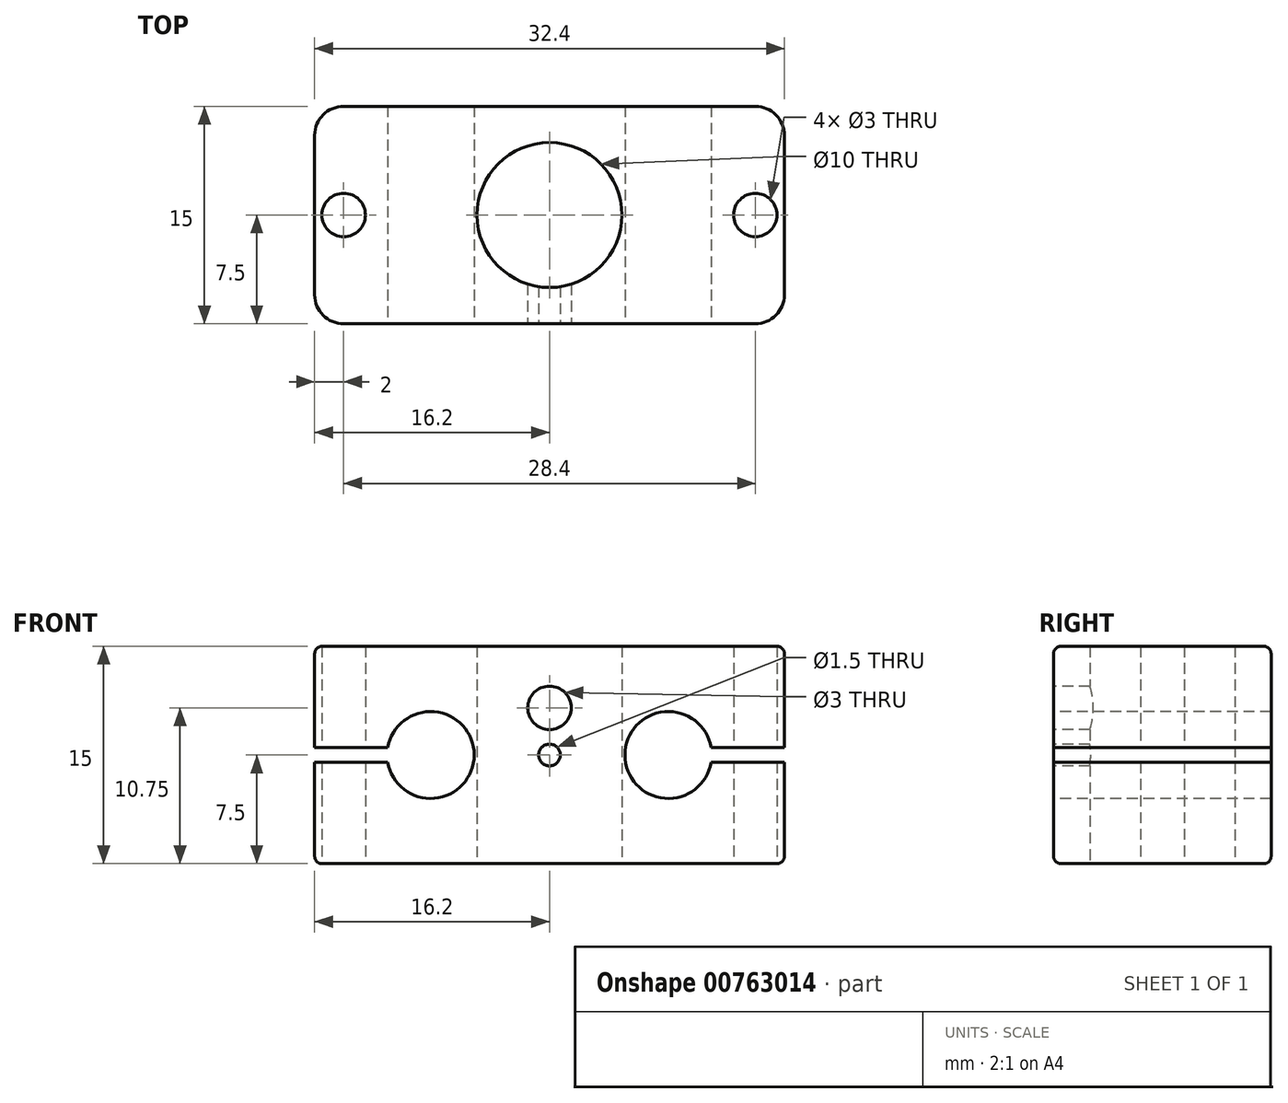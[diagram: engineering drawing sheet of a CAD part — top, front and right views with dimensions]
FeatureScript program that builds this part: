
annotation { "Feature Type Name" : "Feature", "Feature Type Description" : "" }
export const myFeature = defineFeature(function(context is Context, id is Id, definition is map)
    precondition{}
    {
        {
            var Q0;
            Q0=qCreatedBy(makeId("Top.planeOp"),FACE);
            var sketch = newSketch(context, id + "F0", { "sketchPlane" : qUnion([Q0])});
            skCircle(sketch, "E0", {"center": v(0, 0) * mm, "radius": 5 * mm});
            skLineSegment(sketch, "E1.bottom", {"start": v(16.2, 7.5) * mm, "end": v(-16.2, 7.5) * mm});
            skLineSegment(sketch, "E1.top", {"start": v(16.2, -7.5) * mm, "end": v(-16.2, -7.5) * mm});
            skLineSegment(sketch, "E1.left", {"start": v(16.2, 7.5) * mm, "end": v(16.2, -7.5) * mm});
            skLineSegment(sketch, "E1.right", {"start": v(-16.2, 7.5) * mm, "end": v(-16.2, -7.5) * mm});
            skPoint(sketch, "E2", {"position": v(14.2, 0) * mm});
            skPoint(sketch, "E3", {"position": v(-14.2, 0) * mm});
            skSolve(sketch);
        }
        {
            var Q0;
            Q0=makeQuery(id+"F0.imprint","IMPRINT",FACE,{"disambiguationData":[TD([[makeQuery(id+"F0.imprint","IMPRINT",EDGE,{"derivedFrom":sQuery(id+"F0.wireOp",EDGE,"E0")}),-1.0]])]});
            extrude(context, id + "F1", {"entities" : qUnion([Q0]), "depth" : 15 * mm, "offsetDistance" : 25 * mm});
        }
        {
            var Q0;
            Q0=makeQuery(id+"F1.opExtrude","SWEPT_FACE",FACE,{"disambiguationData":[OSD([sQuery(id+"F0.wireOp",EDGE,"E1.top")])]});
            var sketch = newSketch(context, id + "F2", { "sketchPlane" : qUnion([Q0])});
            skCircle(sketch, "E4", {"center": v(8.2, 7.5) * mm, "radius": 3 * mm});
            skCircle(sketch, "E5", {"center": v(-8.2, 7.5) * mm, "radius": 3 * mm});
            skLineSegment(sketch, "E6", {"start": v(-16.2, 7.5) * mm, "end": v(-16.2, 8) * mm});
            skLineSegment(sketch, "E7", {"start": v(-16.2, 8) * mm, "end": v(-16.2, 7) * mm});
            skLineSegment(sketch, "E8", {"start": v(-16.2, 8) * mm, "end": v(-11.16, 8) * mm});
            skLineSegment(sketch, "E9", {"start": v(-16.2, 7) * mm, "end": v(-11.16, 7) * mm});
            skLineSegment(sketch, "E10", {"start": v(16.2, 7.5) * mm, "end": v(16.2, 8) * mm});
            skLineSegment(sketch, "E11", {"start": v(16.2, 8) * mm, "end": v(16.2, 7) * mm});
            skLineSegment(sketch, "E12", {"start": v(16.2, 8) * mm, "end": v(11.16, 8) * mm});
            skLineSegment(sketch, "E13", {"start": v(16.2, 7) * mm, "end": v(11.16, 7) * mm});
            skPoint(sketch, "E14", {"position": v(0, 7.5) * mm});
            skPoint(sketch, "E15", {"position": v(0, 10.75) * mm});
            skSolve(sketch);
        }
        {
            var Q0;
            Q0=sQuery(id+"F2.wireOp",VERTEX,"E5.center");
            var Q1;
            Q1=makeQuery(id+"F1.opExtrude","SWEPT_BODY",BODY,{"disambiguationData":[OSD([sQuery(id+"F0.wireOp",EDGE,"E0"),sQuery(id+"F0.wireOp",EDGE,"E1.bottom"),sQuery(id+"F0.wireOp",EDGE,"E1.top"),sQuery(id+"F0.wireOp",EDGE,"E1.left"),sQuery(id+"F0.wireOp",EDGE,"E1.right")])]});
            hole(context, id + "F3", {"style" : HoleStyle.SIMPLE, "endStyle" : HoleEndStyle.THROUGH, "holeDiameter" : 6 * mm, "majorDiameter" : 5 * mm, "isTappedThrough" : true, "tappedDepth" : 12 * mm, "tapClearance" : 3, "locations" : qUnion([Q0]), "scope" : qUnion([Q1])});
        }
        {
            var Q0;
            Q0=sQuery(id+"F2.wireOp",VERTEX,"E4.center");
            var Q1;
            Q1=makeQuery(id+"F1.opExtrude","SWEPT_BODY",BODY,{"disambiguationData":[OSD([sQuery(id+"F0.wireOp",EDGE,"E0"),sQuery(id+"F0.wireOp",EDGE,"E1.bottom"),sQuery(id+"F0.wireOp",EDGE,"E1.top"),sQuery(id+"F0.wireOp",EDGE,"E1.left"),sQuery(id+"F0.wireOp",EDGE,"E1.right")])]});
            hole(context, id + "F4", {"style" : HoleStyle.SIMPLE, "endStyle" : HoleEndStyle.THROUGH, "holeDiameter" : 6 * mm, "majorDiameter" : 5 * mm, "isTappedThrough" : true, "tappedDepth" : 12 * mm, "tapClearance" : 3, "locations" : qUnion([Q0]), "scope" : qUnion([Q1])});
        }
        {
            var Q0;
            {var subQ0=sQuery(id+"F2.wireOp",EDGE,"E8");Q0=makeQuery(id+"F2.imprint","IMPRINT",FACE,{"disambiguationData":[TD([[makeQuery(id+"F2.imprint","IMPRINT",EDGE,{"derivedFrom":subQ0}),-1.0]])]});}
            extrude(context, id + "F5", {"entities" : qUnion([Q0]), "operationType" : NewBodyOperationType.REMOVE, "endBound" : BoundingType.UP_TO_NEXT, "oppositeDirection" : true, "depth" : 25 * mm, "offsetDistance" : 25 * mm});
        }
        {
            var Q0;
            {var subQ0=sQuery(id+"F2.wireOp",EDGE,"E12");Q0=makeQuery(id+"F2.imprint","IMPRINT",FACE,{"disambiguationData":[TD([[makeQuery(id+"F2.imprint","IMPRINT",EDGE,{"derivedFrom":subQ0}),1.0]])]});}
            extrude(context, id + "F6", {"entities" : qUnion([Q0]), "operationType" : NewBodyOperationType.REMOVE, "endBound" : BoundingType.UP_TO_NEXT, "oppositeDirection" : true, "depth" : 25 * mm, "offsetDistance" : 25 * mm});
        }
        {
            var Q0;
            Q0=sQuery(id+"F0.wireOp",VERTEX,"E3");
            var Q1;
            Q1=sQuery(id+"F0.wireOp",VERTEX,"E2");
            var Q2;
            Q2=makeQuery(id+"F1.opExtrude","SWEPT_BODY",BODY,{"disambiguationData":[OSD([sQuery(id+"F0.wireOp",EDGE,"E0"),sQuery(id+"F0.wireOp",EDGE,"E1.bottom"),sQuery(id+"F0.wireOp",EDGE,"E1.top"),sQuery(id+"F0.wireOp",EDGE,"E1.left"),sQuery(id+"F0.wireOp",EDGE,"E1.right")])]});
            hole(context, id + "F7", {"style" : HoleStyle.SIMPLE, "endStyle" : HoleEndStyle.THROUGH, "oppositeDirection" : true, "holeDiameter" : 3 * mm, "majorDiameter" : 5 * mm, "isTappedThrough" : true, "tappedDepth" : 12 * mm, "tapClearance" : 3, "locations" : qUnion([Q0, Q1]), "scope" : qUnion([Q2])});
        }
        {
            var Q0;
            Q0=sQuery(id+"F2.wireOp",VERTEX,"E14");
            var Q1;
            Q1=makeQuery(id+"F1.opExtrude","SWEPT_BODY",BODY,{"disambiguationData":[OSD([sQuery(id+"F0.wireOp",EDGE,"E0"),sQuery(id+"F0.wireOp",EDGE,"E1.bottom"),sQuery(id+"F0.wireOp",EDGE,"E1.top"),sQuery(id+"F0.wireOp",EDGE,"E1.left"),sQuery(id+"F0.wireOp",EDGE,"E1.right")])]});
            hole(context, id + "F8", {"style" : HoleStyle.SIMPLE, "endStyle" : HoleEndStyle.BLIND, "holeDiameter" : 1.5 * mm, "majorDiameter" : 5 * mm, "holeDepth" : 3 * mm, "isTappedThrough" : true, "tappedDepth" : 12 * mm, "tapClearance" : 3, "locations" : qUnion([Q0]), "scope" : qUnion([Q1])});
        }
        {
            var Q0;
            Q0=sQuery(id+"F2.wireOp",VERTEX,"E15");
            var Q1;
            Q1=makeQuery(id+"F1.opExtrude","SWEPT_BODY",BODY,{"disambiguationData":[OSD([sQuery(id+"F0.wireOp",EDGE,"E0"),sQuery(id+"F0.wireOp",EDGE,"E1.bottom"),sQuery(id+"F0.wireOp",EDGE,"E1.top"),sQuery(id+"F0.wireOp",EDGE,"E1.left"),sQuery(id+"F0.wireOp",EDGE,"E1.right")])]});
            hole(context, id + "F9", {"style" : HoleStyle.SIMPLE, "endStyle" : HoleEndStyle.BLIND, "holeDiameter" : 3 * mm, "majorDiameter" : 5 * mm, "holeDepth" : 3 * mm, "isTappedThrough" : true, "tappedDepth" : 12 * mm, "tapClearance" : 3, "locations" : qUnion([Q0]), "scope" : qUnion([Q1])});
        }
        {
            var Q0;
            {var subQ0=sQuery(id+"F0.wireOp",EDGE,"E1.left");var subQ1=sQuery(id+"F0.wireOp",EDGE,"E1.top");Q0=makeQuery(id+"F6.boolean.opBoolean","SPLIT",EDGE,{"disambiguationData":[TD([makeQuery(id+"F6.opExtrude","SWEPT_FACE",FACE,{"disambiguationData":[OSD([sQuery(id+"F2.wireOp",EDGE,"E12")])]})])],"derivedFrom":makeQuery(id+"F1.opExtrude","SWEPT_EDGE",EDGE,{"disambiguationData":[OSD([subQ1,subQ0])]})});}
            var Q1;
            {var subQ0=sQuery(id+"F0.wireOp",EDGE,"E1.left");var subQ1=sQuery(id+"F0.wireOp",EDGE,"E1.top");Q1=makeQuery(id+"F6.boolean.opBoolean","SPLIT",EDGE,{"disambiguationData":[TD([makeQuery(id+"F6.opExtrude","SWEPT_FACE",FACE,{"disambiguationData":[OSD([sQuery(id+"F2.wireOp",EDGE,"E13")])]})])],"derivedFrom":makeQuery(id+"F1.opExtrude","SWEPT_EDGE",EDGE,{"disambiguationData":[OSD([subQ1,subQ0])]})});}
            var Q2;
            {var subQ0=sQuery(id+"F0.wireOp",EDGE,"E1.left");var subQ1=sQuery(id+"F0.wireOp",EDGE,"E1.bottom");Q2=makeQuery(id+"F6.boolean.opBoolean","SPLIT",EDGE,{"disambiguationData":[TD([makeQuery(id+"F6.opExtrude","SWEPT_FACE",FACE,{"disambiguationData":[OSD([sQuery(id+"F2.wireOp",EDGE,"E12")])]})])],"derivedFrom":makeQuery(id+"F1.opExtrude","SWEPT_EDGE",EDGE,{"disambiguationData":[OSD([subQ1,subQ0])]})});}
            var Q3;
            {var subQ0=sQuery(id+"F0.wireOp",EDGE,"E1.left");var subQ1=sQuery(id+"F0.wireOp",EDGE,"E1.bottom");Q3=makeQuery(id+"F6.boolean.opBoolean","SPLIT",EDGE,{"disambiguationData":[TD([makeQuery(id+"F6.opExtrude","SWEPT_FACE",FACE,{"disambiguationData":[OSD([sQuery(id+"F2.wireOp",EDGE,"E13")])]})])],"derivedFrom":makeQuery(id+"F1.opExtrude","SWEPT_EDGE",EDGE,{"disambiguationData":[OSD([subQ1,subQ0])]})});}
            var Q4;
            {var subQ0=sQuery(id+"F0.wireOp",EDGE,"E1.right");var subQ1=sQuery(id+"F0.wireOp",EDGE,"E1.top");Q4=makeQuery(id+"F5.boolean.opBoolean","SPLIT",EDGE,{"disambiguationData":[TD([makeQuery(id+"F5.opExtrude","SWEPT_FACE",FACE,{"disambiguationData":[OSD([sQuery(id+"F2.wireOp",EDGE,"E9")])]})])],"derivedFrom":makeQuery(id+"F1.opExtrude","SWEPT_EDGE",EDGE,{"disambiguationData":[OSD([subQ1,subQ0])]})});}
            var Q5;
            {var subQ0=sQuery(id+"F0.wireOp",EDGE,"E1.right");var subQ1=sQuery(id+"F0.wireOp",EDGE,"E1.top");Q5=makeQuery(id+"F5.boolean.opBoolean","SPLIT",EDGE,{"disambiguationData":[TD([makeQuery(id+"F5.opExtrude","SWEPT_FACE",FACE,{"disambiguationData":[OSD([sQuery(id+"F2.wireOp",EDGE,"E8")])]})])],"derivedFrom":makeQuery(id+"F1.opExtrude","SWEPT_EDGE",EDGE,{"disambiguationData":[OSD([subQ1,subQ0])]})});}
            var Q6;
            {var subQ0=sQuery(id+"F0.wireOp",EDGE,"E1.right");var subQ1=sQuery(id+"F0.wireOp",EDGE,"E1.bottom");Q6=makeQuery(id+"F5.boolean.opBoolean","SPLIT",EDGE,{"disambiguationData":[TD([makeQuery(id+"F5.opExtrude","SWEPT_FACE",FACE,{"disambiguationData":[OSD([sQuery(id+"F2.wireOp",EDGE,"E9")])]})])],"derivedFrom":makeQuery(id+"F1.opExtrude","SWEPT_EDGE",EDGE,{"disambiguationData":[OSD([subQ1,subQ0])]})});}
            var Q7;
            {var subQ0=sQuery(id+"F0.wireOp",EDGE,"E1.right");var subQ1=sQuery(id+"F0.wireOp",EDGE,"E1.bottom");Q7=makeQuery(id+"F5.boolean.opBoolean","SPLIT",EDGE,{"disambiguationData":[TD([makeQuery(id+"F5.opExtrude","SWEPT_FACE",FACE,{"disambiguationData":[OSD([sQuery(id+"F2.wireOp",EDGE,"E8")])]})])],"derivedFrom":makeQuery(id+"F1.opExtrude","SWEPT_EDGE",EDGE,{"disambiguationData":[OSD([subQ1,subQ0])]})});}
            fillet(context, id + "F10", {"entities" : qUnion([Q0, Q1, Q2, Q3, Q4, Q5, Q6, Q7]), "radius" : 2 * mm, "tangentPropagation" : true, "allowEdgeOverflow" : false});
        }
        {
            var Q0;
            Q0=makeQuery(id+"F1.opExtrude","CAP_EDGE",EDGE,{"disambiguationData":[OSD([sQuery(id+"F0.wireOp",EDGE,"E1.top")])],"isStart":true});
            var Q1;
            Q1=makeQuery(id+"F1.opExtrude","CAP_EDGE",EDGE,{"disambiguationData":[OSD([sQuery(id+"F0.wireOp",EDGE,"E1.bottom")])],"isStart":true});
            var Q2;
            Q2=makeQuery(id+"F1.opExtrude","CAP_EDGE",EDGE,{"disambiguationData":[OSD([sQuery(id+"F0.wireOp",EDGE,"E1.top")])],"isStart":false});
            var Q3;
            Q3=makeQuery(id+"F1.opExtrude","CAP_EDGE",EDGE,{"disambiguationData":[OSD([sQuery(id+"F0.wireOp",EDGE,"E1.bottom")])],"isStart":false});
            fillet(context, id + "F11", {"entities" : qUnion([Q0, Q1, Q2, Q3]), "radius" : 0.5 * mm, "tangentPropagation" : true, "allowEdgeOverflow" : false});
        }
    });
